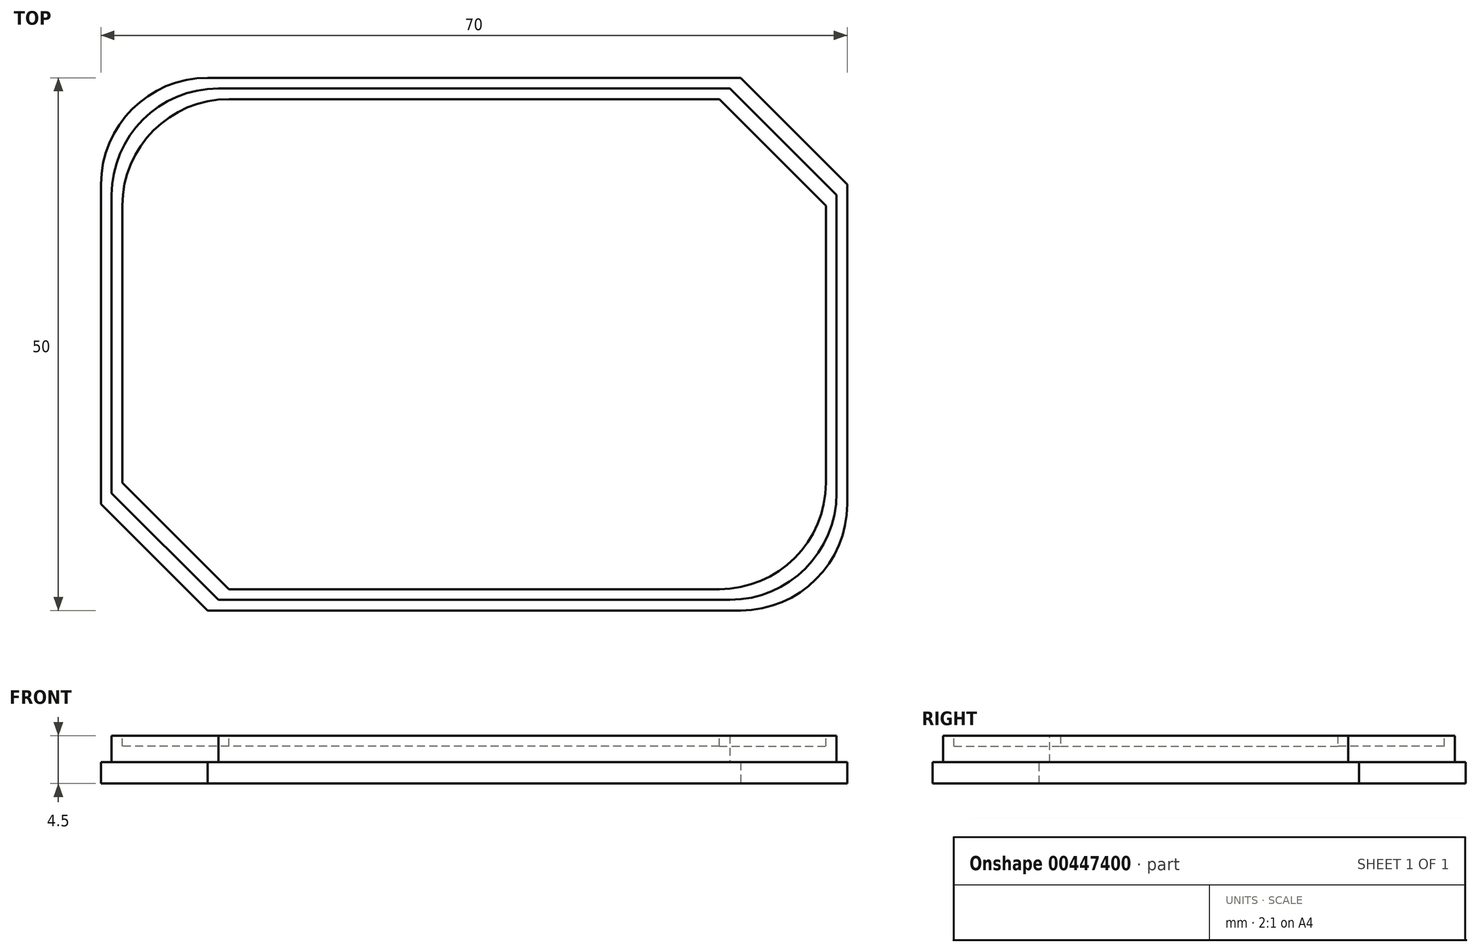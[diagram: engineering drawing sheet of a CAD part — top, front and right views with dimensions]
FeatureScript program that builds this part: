
annotation { "Feature Type Name" : "Feature", "Feature Type Description" : "" }
export const myFeature = defineFeature(function(context is Context, id is Id, definition is map)
    precondition{}
    {
        {
            var Q0;
            Q0=qCreatedBy(makeId("Top.planeOp"),FACE);
            var sketch = newSketch(context, id + "F0", { "sketchPlane" : qUnion([Q0])});
            skLineSegment(sketch, "E0.bottom", {"start": v(35, -25) * mm, "end": v(-35, -25) * mm});
            skLineSegment(sketch, "E0.top", {"start": v(35, 25) * mm, "end": v(-35, 25) * mm});
            skLineSegment(sketch, "E0.left", {"start": v(35, -25) * mm, "end": v(35, 25) * mm});
            skLineSegment(sketch, "E0.right", {"start": v(-35, -25) * mm, "end": v(-35, 25) * mm});
            skPoint(sketch, "E0.middle", {"position": v(0, 0) * mm});
            skSolve(sketch);
        }
        {
            var Q0;
            Q0 = qSketchRegion(id + "F0", true);
            extrude(context, id + "F1", {"entities" : qUnion([Q0]), "depth" : 2 * mm});
        }
        {
            var Q0;
            Q0=makeQuery(id+"F1.opExtrude","CAP_FACE",FACE,{"disambiguationData":[OSD([sQuery(id+"F0.wireOp",EDGE,"E0.bottom"),sQuery(id+"F0.wireOp",EDGE,"E0.top"),sQuery(id+"F0.wireOp",EDGE,"E0.left"),sQuery(id+"F0.wireOp",EDGE,"E0.right")])],"isStart":false});
            var sketch = newSketch(context, id + "F2", { "sketchPlane" : qUnion([Q0])});
            skLineSegment(sketch, "E1.bottom", {"start": v(34, -24) * mm, "end": v(-34, -24) * mm});
            skLineSegment(sketch, "E1.top", {"start": v(34, 24) * mm, "end": v(-34, 24) * mm});
            skLineSegment(sketch, "E1.left", {"start": v(34, -24) * mm, "end": v(34, 24) * mm});
            skLineSegment(sketch, "E1.right", {"start": v(-34, -24) * mm, "end": v(-34, 24) * mm});
            skPoint(sketch, "E1.middle", {"position": v(0, 0) * mm});
            skSolve(sketch);
        }
        {
            var Q0;
            Q0 = qSketchRegion(id + "F2", true);
            extrude(context, id + "F3", {"entities" : qUnion([Q0]), "operationType" : NewBodyOperationType.ADD, "depth" : 2.5 * mm});
        }
        {
            var Q0;
            Q0=makeQuery(id+"F3.opExtrude","CAP_FACE",FACE,{"disambiguationData":[OSD([sQuery(id+"F2.wireOp",EDGE,"E1.bottom"),sQuery(id+"F2.wireOp",EDGE,"E1.top"),sQuery(id+"F2.wireOp",EDGE,"E1.left"),sQuery(id+"F2.wireOp",EDGE,"E1.right")])],"isStart":false});
            var sketch = newSketch(context, id + "F4", { "sketchPlane" : qUnion([Q0])});
            skLineSegment(sketch, "E2.bottom", {"start": v(33, -23) * mm, "end": v(-33, -23) * mm});
            skLineSegment(sketch, "E2.top", {"start": v(33, 23) * mm, "end": v(-33, 23) * mm});
            skLineSegment(sketch, "E2.left", {"start": v(33, -23) * mm, "end": v(33, 23) * mm});
            skLineSegment(sketch, "E2.right", {"start": v(-33, -23) * mm, "end": v(-33, 23) * mm});
            skPoint(sketch, "E2.middle", {"position": v(0, 0) * mm});
            skSolve(sketch);
        }
        {
            var Q0;
            Q0 = qSketchRegion(id + "F4", true);
            extrude(context, id + "F5", {"entities" : qUnion([Q0]), "operationType" : NewBodyOperationType.REMOVE, "oppositeDirection" : true, "depth" : 1 * mm});
        }
        {
            var Q0;
            Q0=makeQuery(id+"F5.boolean.opBoolean","COPY",EDGE,{"derivedFrom":makeQuery(id+"F5.opExtrude","SWEPT_EDGE",EDGE,{"disambiguationData":[OSD([sQuery(id+"F4.wireOp",EDGE,"E2.top"),sQuery(id+"F4.wireOp",EDGE,"E2.left")])]})});
            var Q1;
            Q1=makeQuery(id+"F3.opExtrude","SWEPT_EDGE",EDGE,{"disambiguationData":[OSD([sQuery(id+"F2.wireOp",EDGE,"E1.top"),sQuery(id+"F2.wireOp",EDGE,"E1.left")])]});
            var Q2;
            Q2=makeQuery(id+"F1.opExtrude","SWEPT_EDGE",EDGE,{"disambiguationData":[OSD([sQuery(id+"F0.wireOp",EDGE,"E0.top"),sQuery(id+"F0.wireOp",EDGE,"E0.left")])]});
            var Q3;
            Q3=makeQuery(id+"F5.boolean.opBoolean","COPY",EDGE,{"derivedFrom":makeQuery(id+"F5.opExtrude","SWEPT_EDGE",EDGE,{"disambiguationData":[OSD([sQuery(id+"F4.wireOp",EDGE,"E2.bottom"),sQuery(id+"F4.wireOp",EDGE,"E2.right")])]})});
            var Q4;
            Q4=makeQuery(id+"F3.opExtrude","SWEPT_EDGE",EDGE,{"disambiguationData":[OSD([sQuery(id+"F2.wireOp",EDGE,"E1.bottom"),sQuery(id+"F2.wireOp",EDGE,"E1.right")])]});
            var Q5;
            Q5=makeQuery(id+"F1.opExtrude","SWEPT_EDGE",EDGE,{"disambiguationData":[OSD([sQuery(id+"F0.wireOp",EDGE,"E0.bottom"),sQuery(id+"F0.wireOp",EDGE,"E0.right")])]});
            chamfer(context, id + "F6", {"entities" : qUnion([Q0, Q1, Q2, Q3, Q4, Q5]), "width" : 10 * mm, "tangentPropagation" : true});
        }
        {
            var Q0;
            Q0=makeQuery(id+"F5.boolean.opBoolean","COPY",EDGE,{"derivedFrom":makeQuery(id+"F5.opExtrude","SWEPT_EDGE",EDGE,{"disambiguationData":[OSD([sQuery(id+"F4.wireOp",EDGE,"E2.bottom"),sQuery(id+"F4.wireOp",EDGE,"E2.left")])]})});
            var Q1;
            Q1=makeQuery(id+"F3.opExtrude","SWEPT_EDGE",EDGE,{"disambiguationData":[OSD([sQuery(id+"F2.wireOp",EDGE,"E1.bottom"),sQuery(id+"F2.wireOp",EDGE,"E1.left")])]});
            var Q2;
            Q2=makeQuery(id+"F1.opExtrude","SWEPT_EDGE",EDGE,{"disambiguationData":[OSD([sQuery(id+"F0.wireOp",EDGE,"E0.bottom"),sQuery(id+"F0.wireOp",EDGE,"E0.left")])]});
            var Q3;
            Q3=makeQuery(id+"F5.boolean.opBoolean","COPY",EDGE,{"derivedFrom":makeQuery(id+"F5.opExtrude","SWEPT_EDGE",EDGE,{"disambiguationData":[OSD([sQuery(id+"F4.wireOp",EDGE,"E2.top"),sQuery(id+"F4.wireOp",EDGE,"E2.right")])]})});
            var Q4;
            Q4=makeQuery(id+"F3.opExtrude","SWEPT_EDGE",EDGE,{"disambiguationData":[OSD([sQuery(id+"F2.wireOp",EDGE,"E1.top"),sQuery(id+"F2.wireOp",EDGE,"E1.right")])]});
            var Q5;
            Q5=makeQuery(id+"F1.opExtrude","SWEPT_EDGE",EDGE,{"disambiguationData":[OSD([sQuery(id+"F0.wireOp",EDGE,"E0.top"),sQuery(id+"F0.wireOp",EDGE,"E0.right")])]});
            fillet(context, id + "F7", {"entities" : qUnion([Q0, Q1, Q2, Q3, Q4, Q5]), "radius" : 10 * mm, "tangentPropagation" : true, "allowEdgeOverflow" : false});
        }
    });
